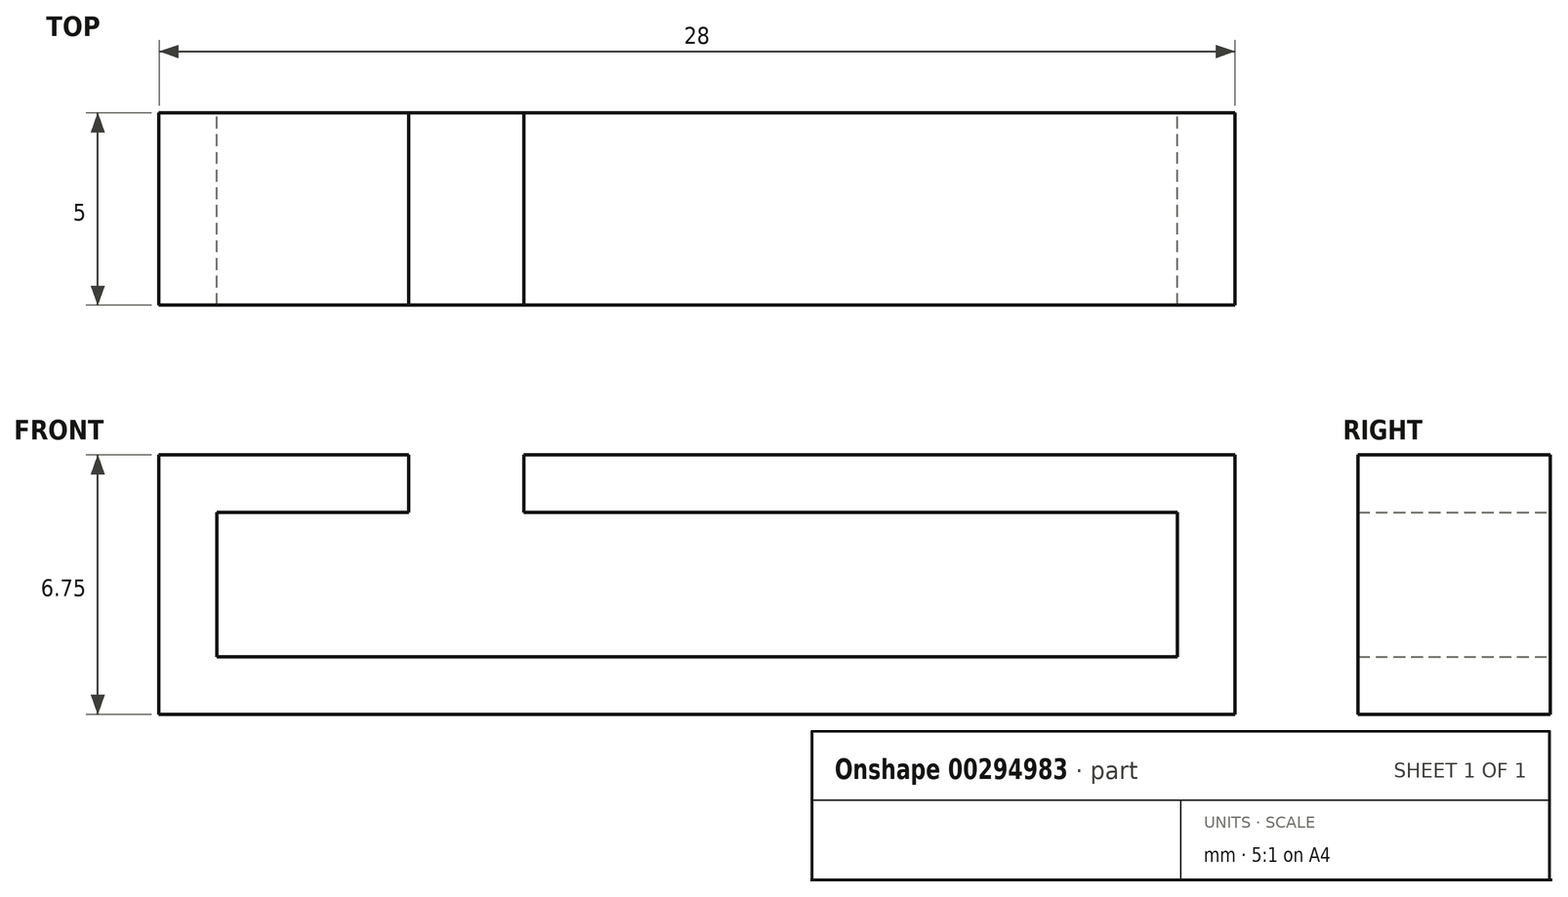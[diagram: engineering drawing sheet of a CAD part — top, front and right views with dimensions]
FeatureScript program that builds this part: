
annotation { "Feature Type Name" : "Feature", "Feature Type Description" : "" }
export const myFeature = defineFeature(function(context is Context, id is Id, definition is map)
    precondition{}
    {
        {
            var Q0;
            Q0=qCreatedBy(makeId("Front.planeOp"),FACE);
            var sketch = newSketch(context, id + "F0", { "sketchPlane" : qUnion([Q0])});
            skLineSegment(sketch, "E0", {"start": v(-49.36, 33.68) * mm, "end": v(-49.36, 26.93) * mm});
            skLineSegment(sketch, "E1", {"start": v(-49.36, 26.93) * mm, "end": v(-21.36, 26.93) * mm});
            skLineSegment(sketch, "E2", {"start": v(-21.36, 26.93) * mm, "end": v(-21.36, 33.68) * mm});
            skLineSegment(sketch, "E3", {"start": v(-21.36, 33.68) * mm, "end": v(-39.86, 33.68) * mm});
            skLineSegment(sketch, "E4", {"start": v(-39.86, 33.68) * mm, "end": v(-39.86, 32.18) * mm});
            skLineSegment(sketch, "E5", {"start": v(-39.86, 32.18) * mm, "end": v(-22.86, 32.18) * mm});
            skLineSegment(sketch, "E6", {"start": v(-22.86, 32.18) * mm, "end": v(-22.86, 28.43) * mm});
            skLineSegment(sketch, "E7", {"start": v(-22.86, 28.43) * mm, "end": v(-47.86, 28.43) * mm});
            skLineSegment(sketch, "E8", {"start": v(-47.86, 28.43) * mm, "end": v(-47.86, 32.18) * mm});
            skLineSegment(sketch, "E9", {"start": v(-47.86, 32.18) * mm, "end": v(-42.86, 32.18) * mm});
            skLineSegment(sketch, "E10", {"start": v(-42.86, 32.18) * mm, "end": v(-42.86, 33.68) * mm});
            skLineSegment(sketch, "E11", {"start": v(-42.86, 33.68) * mm, "end": v(-49.36, 33.68) * mm});
            skSolve(sketch);
        }
        {
            var Q0;
            Q0=makeQuery(id+"F0.imprint","IMPRINT",FACE,{"disambiguationData":[TD([[makeQuery(id+"F0.imprint","IMPRINT",EDGE,{"derivedFrom":sQuery(id+"F0.wireOp",EDGE,"E0")}),1.0]])]});
            extrude(context, id + "F1", {"entities" : qUnion([Q0]), "depth" : 5 * mm});
        }
    });
